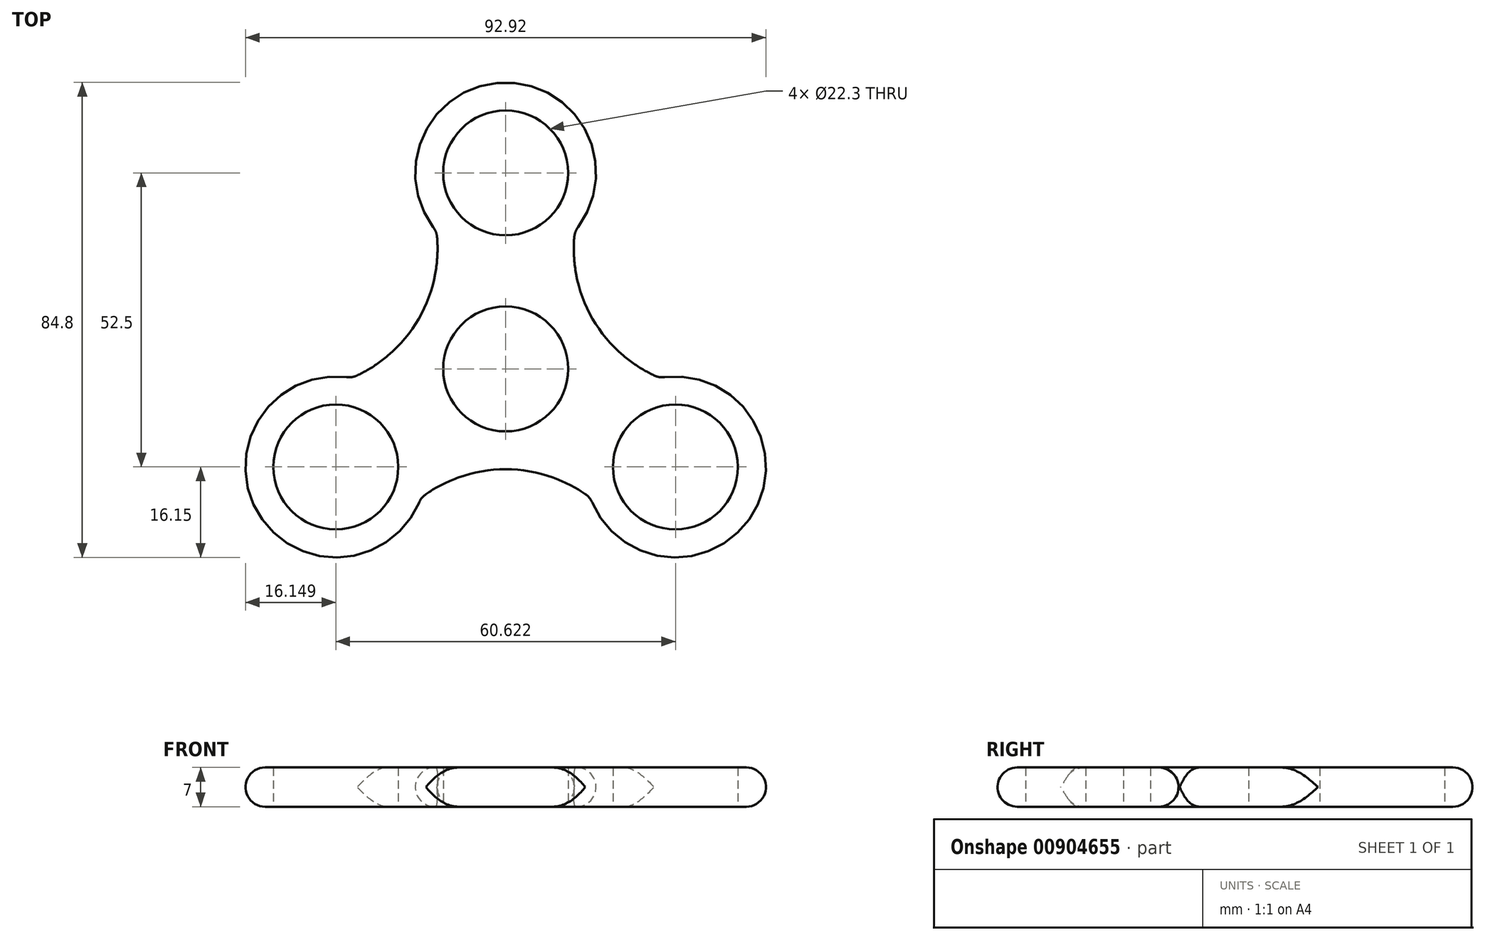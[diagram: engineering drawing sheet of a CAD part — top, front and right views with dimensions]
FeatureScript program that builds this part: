
annotation { "Feature Type Name" : "Feature", "Feature Type Description" : "" }
export const myFeature = defineFeature(function(context is Context, id is Id, definition is map)
    precondition{}
    {
        {
            var Q0;
            Q0=qCreatedBy(makeId("Top.planeOp"),FACE);
            var sketch = newSketch(context, id + "F0", { "sketchPlane" : qUnion([Q0])});
            skCircle(sketch, "E0", {"center": v(0, 0) * mm, "radius": 11.15 * mm});
            skLineSegment(sketch, "E1", {"start": v(0, 0) * mm, "end": v(0, 35) * mm, "construction": true});
            skCircle(sketch, "E2", {"center": v(0, 35) * mm, "radius": 11.15 * mm});
            skCircle(sketch, "E3.1.0", {"center": v(-30.31, -17.5) * mm, "radius": 11.15 * mm});
            skCircle(sketch, "E3.2.0", {"center": v(30.31, -17.5) * mm, "radius": 11.15 * mm});
            skArc(sketch, "E4.0", {"start": v(12.36, 24.6) * mm, "mid": v(0, 51.15) * mm, "end": v(-12.36, 24.6) * mm});
            skArc(sketch, "E5.0", {"start": v(15.13, -23.01) * mm, "mid": v(44.3, -25.58) * mm, "end": v(27.5, -1.6) * mm});
            skArc(sketch, "E6.0", {"start": v(-27.5, -1.6) * mm, "mid": v(-44.3, -25.57) * mm, "end": v(-15.13, -23.01) * mm});
            skLineSegment(sketch, "E7", {"start": v(0, 35) * mm, "end": v(16.15, 35) * mm, "construction": true});
            skLineSegment(sketch, "E8", {"start": v(0, 0) * mm, "end": v(30.31, -17.5) * mm, "construction": true});
            skLineSegment(sketch, "E9", {"start": v(30.31, -17.5) * mm, "end": v(38.39, -3.51) * mm, "construction": true});
            skArc(sketch, "E10", {"start": v(12.36, 24.6) * mm, "mid": v(15.51, 8.96) * mm, "end": v(27.5, -1.6) * mm});
            skArc(sketch, "E11.1.0", {"start": v(-27.5, -1.6) * mm, "mid": v(-15.51, 8.96) * mm, "end": v(-12.36, 24.6) * mm});
            skArc(sketch, "E11.2.0", {"start": v(15.13, -23.01) * mm, "mid": v(0, -17.91) * mm, "end": v(-15.13, -23.01) * mm});
            skPoint(sketch, "E12.orphan", {"position": v(-16.15, 35) * mm});
            skPoint(sketch, "E13.orphan", {"position": v(-38.39, -3.51) * mm});
            skPoint(sketch, "E14.orphan", {"position": v(-22.24, -31.49) * mm});
            skPoint(sketch, "E15.orphan", {"position": v(22.24, -31.49) * mm});
            skSolve(sketch);
        }
        {
            var Q0;
            Q0=qSketchRegion(id+"F0",true);
            extrude(context, id + "F1", {"entities" : qUnion([Q0]), "depth" : 7 * mm, "offsetDistance" : 25 * mm});
        }
        {
            var Q0;
            Q0=makeQuery(id+"F1.opExtrude","SWEPT_FACE",FACE,{"disambiguationData":[OSD([sQuery(id+"F0.wireOp",EDGE,"E5.0")])]});
            var Q1;
            Q1=makeQuery(id+"F1.opExtrude","SWEPT_FACE",FACE,{"disambiguationData":[OSD([sQuery(id+"F0.wireOp",EDGE,"E6.0")])]});
            var Q2;
            Q2=makeQuery(id+"F1.opExtrude","SWEPT_FACE",FACE,{"disambiguationData":[OSD([sQuery(id+"F0.wireOp",EDGE,"E4.0")])]});
            fillet(context, id + "F2", {"entities" : qUnion([Q0, Q1, Q2]), "radius" : 3.5 * mm, "tangentPropagation" : true, "allowEdgeOverflow" : false});
        }
    });
